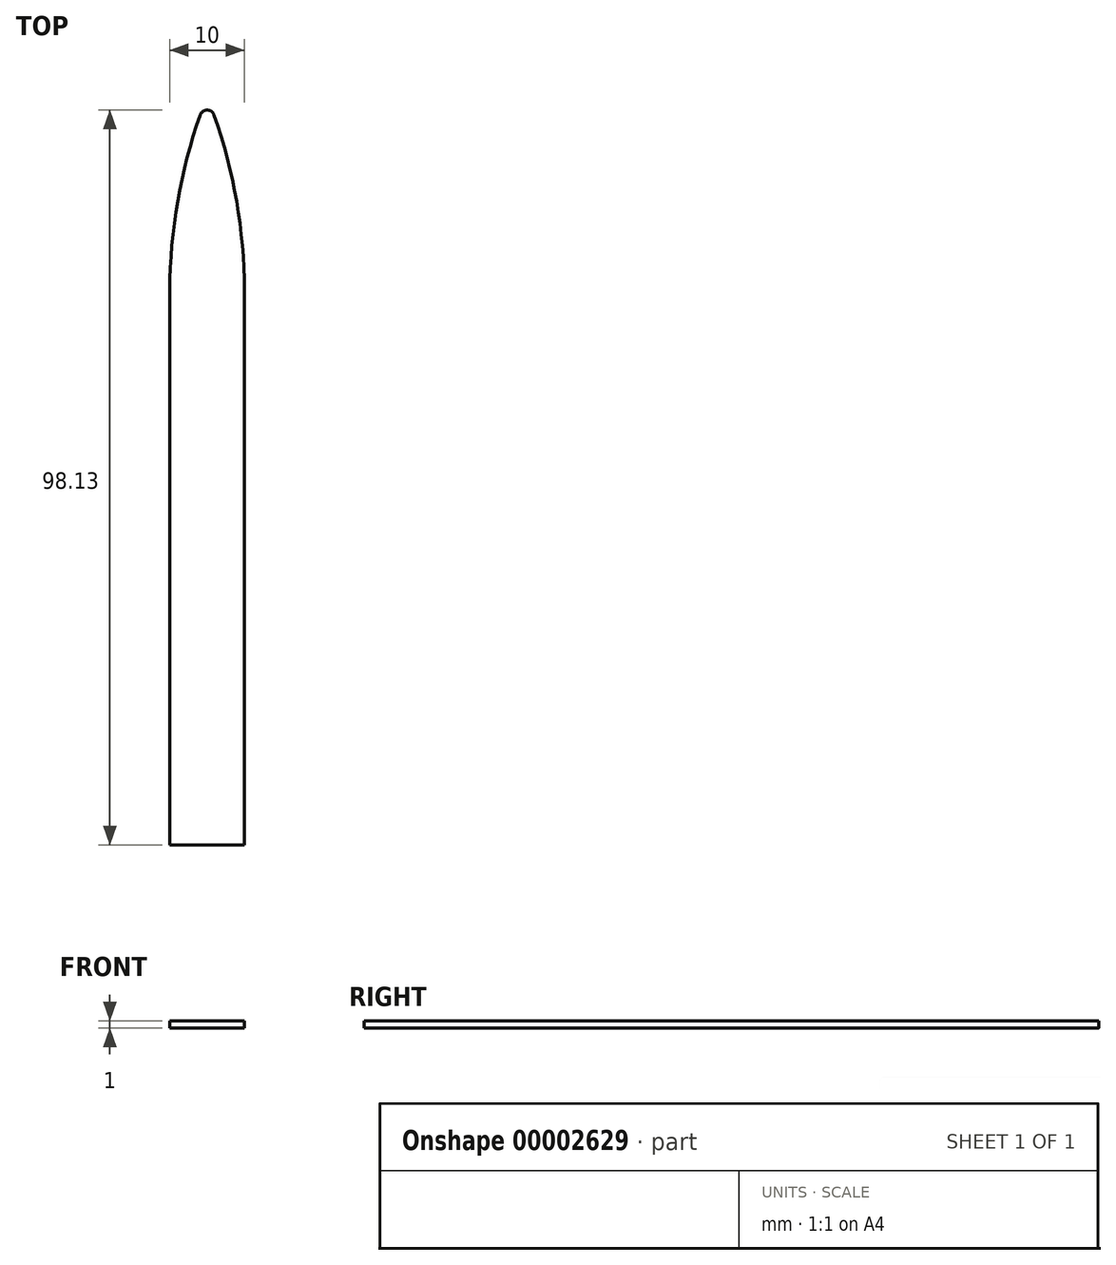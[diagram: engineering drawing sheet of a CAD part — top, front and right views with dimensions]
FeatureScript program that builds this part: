
annotation { "Feature Type Name" : "Feature", "Feature Type Description" : "" }
export const myFeature = defineFeature(function(context is Context, id is Id, definition is map)
    precondition{}
    {
        {
            var Q0;
            Q0=qCreatedBy(makeId("Top.planeOp"),FACE);
            var sketch = newSketch(context, id + "F0", { "sketchPlane" : qUnion([Q0])});
            skLineSegment(sketch, "E0.rect.bottom", {"start": v(5, -50) * mm, "end": v(-5, -50) * mm});
            skLineSegment(sketch, "E0.rect.top", {"start": v(5, 50) * mm, "end": v(-5, 50) * mm});
            skLineSegment(sketch, "E0.rect.left", {"start": v(5, -50) * mm, "end": v(5, 50) * mm});
            skLineSegment(sketch, "E0.rect.right", {"start": v(-5, -50) * mm, "end": v(-5, 50) * mm});
            skPoint(sketch, "E0.rect.middle", {"position": v(0, 0) * mm});
            skArc(sketch, "E1", {"start": v(5, 24.09) * mm, "mid": v(3.94, 35.94) * mm, "end": v(0.94, 47.46) * mm});
            skArc(sketch, "E2.0.MirrorCS", {"start": v(-5, 24.09) * mm, "mid": v(-3.94, 35.94) * mm, "end": v(-0.94, 47.46) * mm});
            skPoint(sketch, "E3.visualSharp", {"position": v(0, 50) * mm});
            skArc(sketch, "E3.filletArc", {"start": v(0.94, 47.46) * mm, "mid": v(0, 48.13) * mm, "end": v(-0.94, 47.46) * mm});
            skSolve(sketch);
        }
        {
            var Q0;
            {var subQ3=sQuery(id+"F0.wireOp",EDGE,"E0.rect.bottom");Q0=makeQuery(id+"F0.imprint","IMPRINT",FACE,{"disambiguationData":[TD([[makeQuery(id+"F0.imprint","IMPRINT",EDGE,{"derivedFrom":subQ3}),-1.0]])]});}
            extrude(context, id + "F1", {"entities" : qUnion([Q0]), "depth" : 1 * mm});
        }
    });
